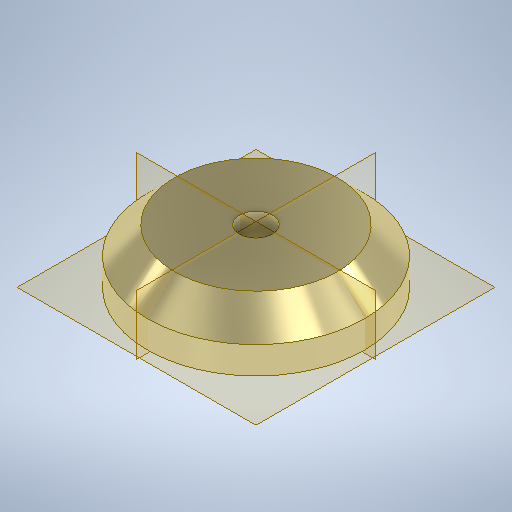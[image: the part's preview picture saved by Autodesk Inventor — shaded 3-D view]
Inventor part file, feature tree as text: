
AUTODESK INVENTOR PART (.ipt)
format: ipt  version: 2025.2 (Build 292293000, 293)  size: 252,928 bytes
history: native  units: mm
features: other x2, sketch x2, extrude x1
ambient origin geometry x8: Origin, YZ Plane, XZ Plane, XY Plane, X Axis, Y Axis, Z Axis, Center Point
bodies: Body1 (feature_tree)
feature tree (5):
  other  "Sólido1"
  other  "Revolução1"
  extrude  "Extrusão1"  Depth=10.0mm
  sketch  "Esboço1"  dims[d0=40.0mm d1=10.0mm]
  sketch  "Esboço2"  dims[d6=135.0deg d7=30.0mm d8=360.0deg d9=12.2mm d10=10.0mm d11=0.0mm]
